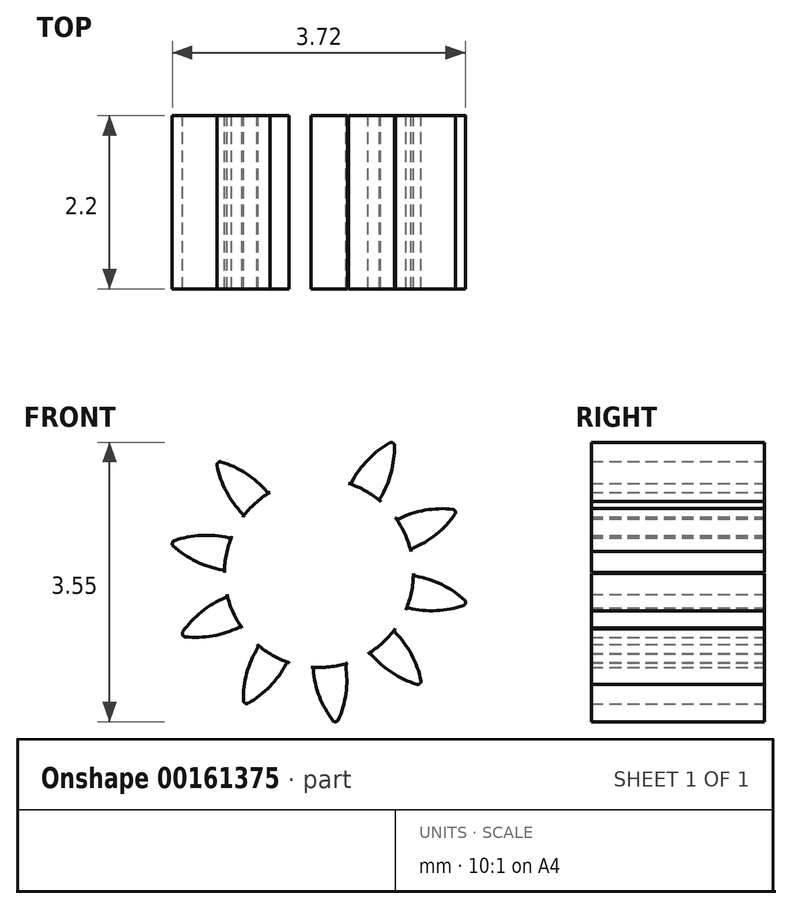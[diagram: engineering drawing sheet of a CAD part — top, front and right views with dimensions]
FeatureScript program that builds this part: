
annotation { "Feature Type Name" : "Feature", "Feature Type Description" : "" }
export const myFeature = defineFeature(function(context is Context, id is Id, definition is map)
    precondition{}
    {
        {
            var Q0;
            Q0=qCreatedBy(makeId("Front.planeOp"),FACE);
            var sketch = newSketch(context, id + "F0", { "sketchPlane" : qUnion([Q0])});
            skCircle(sketch, "E0", {"center": v(0, 0) * mm, "radius": 1.2 * mm, "construction": true});
            skCircle(sketch, "E1", {"center": v(0, 0) * mm, "radius": 1.55 * mm, "construction": true});
            skCircle(sketch, "E2", {"center": v(0, 0) * mm, "radius": 1.9 * mm, "construction": true});
            skLineSegment(sketch, "E3", {"start": v(0, 8.23) * mm, "end": v(0, 0) * mm, "construction": true});
            skCircle(sketch, "E4.cCircle", {"center": v(0, 0) * mm, "radius": 8.23 * mm, "construction": true});
            skLineSegment(sketch, "E4.0", {"start": v(0, 8.23) * mm, "end": v(1.83, 8.03) * mm, "construction": true});
            skLineSegment(sketch, "E4.1", {"start": v(1.83, 8.03) * mm, "end": v(3.57, 7.42) * mm, "construction": true});
            skLineSegment(sketch, "E4.2", {"start": v(3.57, 7.42) * mm, "end": v(5.13, 6.44) * mm, "construction": true});
            skLineSegment(sketch, "E4.3", {"start": v(5.13, 6.44) * mm, "end": v(6.44, 5.13) * mm, "construction": true});
            skLineSegment(sketch, "E4.4", {"start": v(6.44, 5.13) * mm, "end": v(7.42, 3.57) * mm, "construction": true});
            skLineSegment(sketch, "E4.5", {"start": v(7.42, 3.57) * mm, "end": v(8.03, 1.83) * mm, "construction": true});
            skLineSegment(sketch, "E4.6", {"start": v(8.03, 1.83) * mm, "end": v(8.23, 0) * mm, "construction": true});
            skLineSegment(sketch, "E4.7", {"start": v(8.23, 0) * mm, "end": v(8.03, -1.83) * mm, "construction": true});
            skLineSegment(sketch, "E4.8", {"start": v(8.03, -1.83) * mm, "end": v(7.42, -3.57) * mm, "construction": true});
            skLineSegment(sketch, "E4.9", {"start": v(7.42, -3.57) * mm, "end": v(6.44, -5.13) * mm, "construction": true});
            skLineSegment(sketch, "E4.10", {"start": v(6.44, -5.13) * mm, "end": v(5.13, -6.44) * mm, "construction": true});
            skLineSegment(sketch, "E4.11", {"start": v(5.13, -6.44) * mm, "end": v(3.57, -7.42) * mm, "construction": true});
            skLineSegment(sketch, "E4.12", {"start": v(3.57, -7.42) * mm, "end": v(1.83, -8.03) * mm, "construction": true});
            skLineSegment(sketch, "E4.13", {"start": v(1.83, -8.03) * mm, "end": v(0, -8.23) * mm, "construction": true});
            skLineSegment(sketch, "E4.14", {"start": v(0, -8.23) * mm, "end": v(-1.83, -8.03) * mm, "construction": true});
            skLineSegment(sketch, "E4.15", {"start": v(-1.83, -8.03) * mm, "end": v(-3.57, -7.42) * mm, "construction": true});
            skLineSegment(sketch, "E4.16", {"start": v(-3.57, -7.42) * mm, "end": v(-5.13, -6.44) * mm, "construction": true});
            skLineSegment(sketch, "E4.17", {"start": v(-5.13, -6.44) * mm, "end": v(-6.44, -5.13) * mm, "construction": true});
            skLineSegment(sketch, "E4.18", {"start": v(-6.44, -5.13) * mm, "end": v(-7.42, -3.57) * mm, "construction": true});
            skLineSegment(sketch, "E4.19", {"start": v(-7.42, -3.57) * mm, "end": v(-8.03, -1.83) * mm, "construction": true});
            skLineSegment(sketch, "E4.20", {"start": v(-8.03, -1.83) * mm, "end": v(-8.23, 0) * mm, "construction": true});
            skLineSegment(sketch, "E4.21", {"start": v(-8.23, 0) * mm, "end": v(-8.03, 1.83) * mm, "construction": true});
            skLineSegment(sketch, "E4.22", {"start": v(-8.03, 1.83) * mm, "end": v(-7.42, 3.57) * mm, "construction": true});
            skLineSegment(sketch, "E4.23", {"start": v(-7.42, 3.57) * mm, "end": v(-6.44, 5.13) * mm, "construction": true});
            skLineSegment(sketch, "E4.24", {"start": v(-6.44, 5.13) * mm, "end": v(-5.13, 6.44) * mm, "construction": true});
            skLineSegment(sketch, "E4.25", {"start": v(-5.13, 6.44) * mm, "end": v(-3.57, 7.42) * mm, "construction": true});
            skLineSegment(sketch, "E4.26", {"start": v(-3.57, 7.42) * mm, "end": v(-1.83, 8.03) * mm, "construction": true});
            skLineSegment(sketch, "E4.27", {"start": v(-1.83, 8.03) * mm, "end": v(0, 8.23) * mm, "construction": true});
            skLineSegment(sketch, "E5.0", {"start": v(-0.93, 8.23) * mm, "end": v(0.93, 8.23) * mm, "construction": true});
            skLineSegment(sketch, "E5.1", {"start": v(0.93, 8.23) * mm, "end": v(2.74, 7.82) * mm, "construction": true});
            skLineSegment(sketch, "E5.2", {"start": v(2.74, 7.82) * mm, "end": v(4.4, 7.02) * mm, "construction": true});
            skLineSegment(sketch, "E5.3", {"start": v(4.4, 7.02) * mm, "end": v(5.86, 5.86) * mm});
            skLineSegment(sketch, "E5.4", {"start": v(5.86, 5.86) * mm, "end": v(7.02, 4.4) * mm});
            skLineSegment(sketch, "E5.5", {"start": v(7.02, 4.4) * mm, "end": v(7.82, 2.74) * mm});
            skLineSegment(sketch, "E5.6", {"start": v(7.82, 2.74) * mm, "end": v(8.23, 0.93) * mm});
            skLineSegment(sketch, "E5.7", {"start": v(8.23, 0.93) * mm, "end": v(8.23, -0.93) * mm});
            skLineSegment(sketch, "E5.8", {"start": v(8.23, -0.93) * mm, "end": v(7.82, -2.74) * mm});
            skLineSegment(sketch, "E5.9", {"start": v(7.82, -2.74) * mm, "end": v(7.02, -4.4) * mm});
            skLineSegment(sketch, "E5.10", {"start": v(7.02, -4.4) * mm, "end": v(5.86, -5.86) * mm});
            skLineSegment(sketch, "E5.11", {"start": v(5.86, -5.86) * mm, "end": v(4.4, -7.02) * mm});
            skLineSegment(sketch, "E5.12", {"start": v(4.4, -7.02) * mm, "end": v(2.74, -7.82) * mm});
            skLineSegment(sketch, "E5.13", {"start": v(2.74, -7.82) * mm, "end": v(0.93, -8.23) * mm});
            skLineSegment(sketch, "E5.14", {"start": v(0.93, -8.23) * mm, "end": v(-0.93, -8.23) * mm});
            skLineSegment(sketch, "E5.15", {"start": v(-0.93, -8.23) * mm, "end": v(-2.74, -7.82) * mm});
            skLineSegment(sketch, "E5.16", {"start": v(-2.74, -7.82) * mm, "end": v(-4.4, -7.02) * mm});
            skLineSegment(sketch, "E5.17", {"start": v(-4.4, -7.02) * mm, "end": v(-5.86, -5.86) * mm});
            skLineSegment(sketch, "E5.18", {"start": v(-5.86, -5.86) * mm, "end": v(-7.02, -4.4) * mm});
            skLineSegment(sketch, "E5.19", {"start": v(-7.02, -4.4) * mm, "end": v(-7.82, -2.74) * mm});
            skLineSegment(sketch, "E5.20", {"start": v(-7.82, -2.74) * mm, "end": v(-8.23, -0.93) * mm});
            skLineSegment(sketch, "E5.21", {"start": v(-8.23, -0.93) * mm, "end": v(-8.23, 0.93) * mm});
            skLineSegment(sketch, "E5.22", {"start": v(-8.23, 0.93) * mm, "end": v(-7.82, 2.74) * mm});
            skLineSegment(sketch, "E5.23", {"start": v(-7.82, 2.74) * mm, "end": v(-7.02, 4.4) * mm});
            skLineSegment(sketch, "E5.24", {"start": v(-7.02, 4.4) * mm, "end": v(-5.86, 5.86) * mm});
            skLineSegment(sketch, "E5.25", {"start": v(-5.86, 5.86) * mm, "end": v(-4.4, 7.02) * mm, "construction": true});
            skLineSegment(sketch, "E5.26", {"start": v(-4.4, 7.02) * mm, "end": v(-2.74, 7.82) * mm, "construction": true});
            skLineSegment(sketch, "E5.27", {"start": v(-2.74, 7.82) * mm, "end": v(-0.93, 8.23) * mm, "construction": true});
            skPoint(sketch, "E5.0.midPoint", {"position": v(0, 8.23) * mm});
            skLineSegment(sketch, "E6", {"start": v(-0.93, 8.23) * mm, "end": v(0, 0) * mm, "construction": true});
            skLineSegment(sketch, "E7", {"start": v(0, 1.55) * mm, "end": v(-9.32, 1.55) * mm, "construction": true});
            skLineSegment(sketch, "E8", {"start": v(0, 1.55) * mm, "end": v(-4.26, 0) * mm, "construction": true});
            skCircle(sketch, "E9", {"center": v(0, 1.55) * mm, "radius": 1.25 * mm, "construction": true});
            skCircle(sketch, "E10", {"center": v(-1.17, 1.12) * mm, "radius": 1.25 * mm, "construction": true});
            skArc(sketch, "E11", {"start": v(-0.18, 1.88) * mm, "mid": v(0, 1.57) * mm, "end": v(0.07, 1.22) * mm});
            skArc(sketch, "E12.MirrorCS", {"start": v(-0.24, 1.89) * mm, "mid": v(-0.34, 1.53) * mm, "end": v(-0.34, 1.15) * mm});
            skArc(sketch, "E13.MirrorCS", {"start": v(-0.24, 1.87) * mm, "mid": v(-0.34, 1.53) * mm, "end": v(-0.34, 1.18) * mm});
            skArc(sketch, "E14", {"start": v(-0.22, 1.89) * mm, "mid": v(-0.21, 1.89) * mm, "end": v(-0.2, 1.89) * mm});
            skArc(sketch, "E15", {"start": v(-0.36, 1.14) * mm, "mid": v(0.13, -1.2) * mm, "end": v(0.1, 1.2) * mm});
            skPoint(sketch, "E16.visualSharp", {"position": v(-0.34, 1.15) * mm});
            skArc(sketch, "E16.filletArc", {"start": v(-0.36, 1.14) * mm, "mid": v(-0.35, 1.16) * mm, "end": v(-0.34, 1.18) * mm});
            skPoint(sketch, "E17.visualSharp", {"position": v(0.07, 1.2) * mm});
            skArc(sketch, "E17.filletArc", {"start": v(0.07, 1.22) * mm, "mid": v(0.08, 1.2) * mm, "end": v(0.1, 1.2) * mm});
            skPoint(sketch, "E18.visualSharp", {"position": v(-0.24, 1.89) * mm});
            skArc(sketch, "E18.filletArc", {"start": v(-0.22, 1.89) * mm, "mid": v(-0.23, 1.88) * mm, "end": v(-0.24, 1.87) * mm});
            skPoint(sketch, "E19.visualSharp", {"position": v(-0.19, 1.9) * mm});
            skArc(sketch, "E19.filletArc", {"start": v(-0.18, 1.88) * mm, "mid": v(-0.2, 1.89) * mm, "end": v(-0.2, 1.89) * mm});
            skArc(sketch, "E20.1.0", {"start": v(-1.3, 1.37) * mm, "mid": v(-1.18, 1.04) * mm, "end": v(-0.97, 0.75) * mm});
            skArc(sketch, "E20.1.1", {"start": v(-0.97, 0.71) * mm, "mid": v(-0.96, 0.73) * mm, "end": v(-0.97, 0.75) * mm});
            skArc(sketch, "E20.1.2", {"start": v(-1.29, 1.4) * mm, "mid": v(-1.3, 1.38) * mm, "end": v(-1.3, 1.37) * mm});
            skArc(sketch, "E20.1.3", {"start": v(-1.29, 1.4) * mm, "mid": v(-1.28, 1.4) * mm, "end": v(-1.28, 1.4) * mm});
            skArc(sketch, "E20.1.4", {"start": v(-1.25, 1.41) * mm, "mid": v(-0.93, 1.26) * mm, "end": v(-0.66, 1.03) * mm});
            skArc(sketch, "E20.1.5", {"start": v(-1.25, 1.41) * mm, "mid": v(-1.26, 1.41) * mm, "end": v(-1.28, 1.4) * mm});
            skArc(sketch, "E20.1.6", {"start": v(-0.66, 1.03) * mm, "mid": v(-0.64, 1.02) * mm, "end": v(-0.62, 1.03) * mm});
            skArc(sketch, "E20.2.0", {"start": v(-1.85, 0.35) * mm, "mid": v(-1.56, 0.15) * mm, "end": v(-1.23, 0.04) * mm});
            skArc(sketch, "E20.2.1", {"start": v(-1.2, 0) * mm, "mid": v(-1.2, 0.03) * mm, "end": v(-1.23, 0.04) * mm});
            skArc(sketch, "E20.2.2", {"start": v(-1.86, 0.37) * mm, "mid": v(-1.86, 0.36) * mm, "end": v(-1.85, 0.35) * mm});
            skArc(sketch, "E20.2.3", {"start": v(-1.86, 0.37) * mm, "mid": v(-1.86, 0.38) * mm, "end": v(-1.86, 0.39) * mm});
            skArc(sketch, "E20.2.4", {"start": v(-1.84, 0.41) * mm, "mid": v(-1.5, 0.48) * mm, "end": v(-1.14, 0.45) * mm});
            skArc(sketch, "E20.2.5", {"start": v(-1.84, 0.41) * mm, "mid": v(-1.85, 0.4) * mm, "end": v(-1.86, 0.39) * mm});
            skArc(sketch, "E20.2.6", {"start": v(-1.14, 0.45) * mm, "mid": v(-1.12, 0.45) * mm, "end": v(-1.1, 0.46) * mm});
            skArc(sketch, "E20.3.0", {"start": v(-1.7, -0.8) * mm, "mid": v(-1.35, -0.8) * mm, "end": v(-1.01, -0.69) * mm});
            skArc(sketch, "E20.3.1", {"start": v(-0.98, -0.7) * mm, "mid": v(-1, -0.69) * mm, "end": v(-1.01, -0.69) * mm});
            skArc(sketch, "E20.3.2", {"start": v(-1.73, -0.8) * mm, "mid": v(-1.72, -0.8) * mm, "end": v(-1.7, -0.8) * mm});
            skArc(sketch, "E20.3.3", {"start": v(-1.73, -0.8) * mm, "mid": v(-1.73, -0.79) * mm, "end": v(-1.73, -0.78) * mm});
            skArc(sketch, "E20.3.4", {"start": v(-1.73, -0.75) * mm, "mid": v(-1.49, -0.5) * mm, "end": v(-1.19, -0.31) * mm});
            skArc(sketch, "E20.3.5", {"start": v(-1.73, -0.75) * mm, "mid": v(-1.74, -0.76) * mm, "end": v(-1.73, -0.78) * mm});
            skArc(sketch, "E20.3.6", {"start": v(-1.19, -0.31) * mm, "mid": v(-1.17, -0.3) * mm, "end": v(-1.17, -0.27) * mm});
            skArc(sketch, "E20.4.0", {"start": v(-0.9, -1.66) * mm, "mid": v(-0.62, -1.44) * mm, "end": v(-0.42, -1.15) * mm});
            skArc(sketch, "E20.4.1", {"start": v(-0.38, -1.14) * mm, "mid": v(-0.4, -1.14) * mm, "end": v(-0.42, -1.15) * mm});
            skArc(sketch, "E20.4.2", {"start": v(-0.93, -1.66) * mm, "mid": v(-0.92, -1.66) * mm, "end": v(-0.9, -1.66) * mm});
            skArc(sketch, "E20.4.3", {"start": v(-0.93, -1.66) * mm, "mid": v(-0.94, -1.65) * mm, "end": v(-0.94, -1.65) * mm});
            skArc(sketch, "E20.4.4", {"start": v(-0.96, -1.62) * mm, "mid": v(-0.92, -1.27) * mm, "end": v(-0.78, -0.95) * mm});
            skArc(sketch, "E20.4.5", {"start": v(-0.96, -1.62) * mm, "mid": v(-0.95, -1.64) * mm, "end": v(-0.94, -1.65) * mm});
            skArc(sketch, "E20.4.6", {"start": v(-0.78, -0.95) * mm, "mid": v(-0.77, -0.93) * mm, "end": v(-0.78, -0.9) * mm});
            skArc(sketch, "E20.5.0", {"start": v(0.24, -1.87) * mm, "mid": v(0.34, -1.53) * mm, "end": v(0.34, -1.18) * mm});
            skArc(sketch, "E20.5.1", {"start": v(0.36, -1.14) * mm, "mid": v(0.35, -1.16) * mm, "end": v(0.34, -1.18) * mm});
            skArc(sketch, "E20.5.2", {"start": v(0.22, -1.89) * mm, "mid": v(0.23, -1.88) * mm, "end": v(0.24, -1.87) * mm});
            skArc(sketch, "E20.5.3", {"start": v(0.22, -1.89) * mm, "mid": v(0.21, -1.89) * mm, "end": v(0.2, -1.89) * mm});
            skArc(sketch, "E20.5.4", {"start": v(0.18, -1.88) * mm, "mid": v(0, -1.57) * mm, "end": v(-0.07, -1.22) * mm});
            skArc(sketch, "E20.5.5", {"start": v(0.18, -1.88) * mm, "mid": v(0.2, -1.89) * mm, "end": v(0.2, -1.89) * mm});
            skArc(sketch, "E20.5.6", {"start": v(-0.07, -1.22) * mm, "mid": v(-0.08, -1.2) * mm, "end": v(-0.1, -1.2) * mm});
            skArc(sketch, "E20.6.0", {"start": v(1.3, -1.37) * mm, "mid": v(1.18, -1.04) * mm, "end": v(0.97, -0.75) * mm});
            skArc(sketch, "E20.6.1", {"start": v(0.97, -0.71) * mm, "mid": v(0.96, -0.73) * mm, "end": v(0.97, -0.75) * mm});
            skArc(sketch, "E20.6.2", {"start": v(1.29, -1.4) * mm, "mid": v(1.3, -1.38) * mm, "end": v(1.3, -1.37) * mm});
            skArc(sketch, "E20.6.3", {"start": v(1.29, -1.4) * mm, "mid": v(1.28, -1.4) * mm, "end": v(1.28, -1.4) * mm});
            skArc(sketch, "E20.6.4", {"start": v(1.25, -1.41) * mm, "mid": v(0.93, -1.26) * mm, "end": v(0.66, -1.03) * mm});
            skArc(sketch, "E20.6.5", {"start": v(1.25, -1.41) * mm, "mid": v(1.26, -1.41) * mm, "end": v(1.28, -1.4) * mm});
            skArc(sketch, "E20.6.6", {"start": v(0.66, -1.03) * mm, "mid": v(0.64, -1.02) * mm, "end": v(0.62, -1.03) * mm});
            skArc(sketch, "E20.7.0", {"start": v(1.85, -0.35) * mm, "mid": v(1.56, -0.15) * mm, "end": v(1.23, -0.04) * mm});
            skArc(sketch, "E20.7.1", {"start": v(1.2, 0) * mm, "mid": v(1.2, -0.03) * mm, "end": v(1.23, -0.04) * mm});
            skArc(sketch, "E20.7.2", {"start": v(1.86, -0.37) * mm, "mid": v(1.86, -0.36) * mm, "end": v(1.85, -0.35) * mm});
            skArc(sketch, "E20.7.3", {"start": v(1.86, -0.37) * mm, "mid": v(1.86, -0.38) * mm, "end": v(1.86, -0.39) * mm});
            skArc(sketch, "E20.7.4", {"start": v(1.84, -0.41) * mm, "mid": v(1.5, -0.48) * mm, "end": v(1.14, -0.45) * mm});
            skArc(sketch, "E20.7.5", {"start": v(1.84, -0.41) * mm, "mid": v(1.85, -0.4) * mm, "end": v(1.86, -0.39) * mm});
            skArc(sketch, "E20.7.6", {"start": v(1.14, -0.45) * mm, "mid": v(1.12, -0.45) * mm, "end": v(1.1, -0.46) * mm});
            skArc(sketch, "E20.8.0", {"start": v(1.7, 0.8) * mm, "mid": v(1.35, 0.8) * mm, "end": v(1.01, 0.69) * mm});
            skArc(sketch, "E20.8.1", {"start": v(0.98, 0.7) * mm, "mid": v(1, 0.69) * mm, "end": v(1.01, 0.69) * mm});
            skArc(sketch, "E20.8.2", {"start": v(1.73, 0.8) * mm, "mid": v(1.72, 0.8) * mm, "end": v(1.7, 0.8) * mm});
            skArc(sketch, "E20.8.3", {"start": v(1.73, 0.8) * mm, "mid": v(1.73, 0.79) * mm, "end": v(1.73, 0.78) * mm});
            skArc(sketch, "E20.8.4", {"start": v(1.73, 0.75) * mm, "mid": v(1.49, 0.5) * mm, "end": v(1.19, 0.31) * mm});
            skArc(sketch, "E20.8.5", {"start": v(1.73, 0.75) * mm, "mid": v(1.74, 0.76) * mm, "end": v(1.73, 0.78) * mm});
            skArc(sketch, "E20.8.6", {"start": v(1.19, 0.31) * mm, "mid": v(1.17, 0.3) * mm, "end": v(1.17, 0.27) * mm});
            skArc(sketch, "E20.9.0", {"start": v(0.9, 1.66) * mm, "mid": v(0.62, 1.44) * mm, "end": v(0.42, 1.15) * mm});
            skArc(sketch, "E20.9.1", {"start": v(0.38, 1.14) * mm, "mid": v(0.4, 1.14) * mm, "end": v(0.42, 1.15) * mm});
            skArc(sketch, "E20.9.2", {"start": v(0.93, 1.66) * mm, "mid": v(0.92, 1.66) * mm, "end": v(0.9, 1.66) * mm});
            skArc(sketch, "E20.9.3", {"start": v(0.93, 1.66) * mm, "mid": v(0.94, 1.65) * mm, "end": v(0.94, 1.65) * mm});
            skArc(sketch, "E20.9.4", {"start": v(0.96, 1.62) * mm, "mid": v(0.92, 1.27) * mm, "end": v(0.78, 0.95) * mm});
            skArc(sketch, "E20.9.5", {"start": v(0.96, 1.62) * mm, "mid": v(0.95, 1.64) * mm, "end": v(0.94, 1.65) * mm});
            skArc(sketch, "E20.9.6", {"start": v(0.78, 0.95) * mm, "mid": v(0.77, 0.93) * mm, "end": v(0.78, 0.9) * mm});
            skSolve(sketch);
        }
        {
            var Q0;
            Q0=makeQuery(id+"F0.imprint","IMPRINT",FACE,{"disambiguationData":[TD([[makeQuery(id+"F0.imprint","IMPRINT",EDGE,{"derivedFrom":sQuery(id+"F0.wireOp",EDGE,"E11")}),-1.0]])]});
            var Q1;
            Q1=makeQuery(id+"F0.imprint","IMPRINT",FACE,{"disambiguationData":[TD([[makeQuery(id+"F0.imprint","IMPRINT",EDGE,{"derivedFrom":sQuery(id+"F0.wireOp",EDGE,"E20.1.0")}),1.0]])]});
            var Q2;
            Q2=makeQuery(id+"F0.imprint","IMPRINT",FACE,{"disambiguationData":[TD([[makeQuery(id+"F0.imprint","IMPRINT",EDGE,{"derivedFrom":sQuery(id+"F0.wireOp",EDGE,"E20.3.0")}),1.0]])]});
            var Q3;
            Q3=makeQuery(id+"F0.imprint","IMPRINT",FACE,{"disambiguationData":[TD([[makeQuery(id+"F0.imprint","IMPRINT",EDGE,{"derivedFrom":sQuery(id+"F0.wireOp",EDGE,"E20.5.0")}),1.0]])]});
            var Q4;
            Q4=makeQuery(id+"F0.imprint","IMPRINT",FACE,{"disambiguationData":[TD([[makeQuery(id+"F0.imprint","IMPRINT",EDGE,{"derivedFrom":sQuery(id+"F0.wireOp",EDGE,"E20.6.0")}),1.0]])]});
            var Q5;
            Q5=makeQuery(id+"F0.imprint","IMPRINT",FACE,{"disambiguationData":[TD([[makeQuery(id+"F0.imprint","IMPRINT",EDGE,{"derivedFrom":sQuery(id+"F0.wireOp",EDGE,"E20.7.0")}),1.0]])]});
            var Q6;
            Q6=makeQuery(id+"F0.imprint","IMPRINT",FACE,{"disambiguationData":[TD([[makeQuery(id+"F0.imprint","IMPRINT",EDGE,{"derivedFrom":sQuery(id+"F0.wireOp",EDGE,"E20.8.0")}),1.0]])]});
            var Q7;
            Q7=makeQuery(id+"F0.imprint","IMPRINT",FACE,{"disambiguationData":[TD([[makeQuery(id+"F0.imprint","IMPRINT",EDGE,{"derivedFrom":sQuery(id+"F0.wireOp",EDGE,"E20.9.0")}),1.0]])]});
            var Q8;
            Q8=makeQuery(id+"F0.imprint","IMPRINT",FACE,{"disambiguationData":[TD([[makeQuery(id+"F0.imprint","IMPRINT",EDGE,{"derivedFrom":sQuery(id+"F0.wireOp",EDGE,"E20.10.0")}),1.0]])]});
            var Q9;
            Q9=makeQuery(id+"F0.imprint","IMPRINT",FACE,{"disambiguationData":[TD([[makeQuery(id+"F0.imprint","IMPRINT",EDGE,{"derivedFrom":sQuery(id+"F0.wireOp",EDGE,"E20.11.0")}),1.0]])]});
            var Q10;
            Q10=makeQuery(id+"F0.imprint","IMPRINT",FACE,{"disambiguationData":[TD([[makeQuery(id+"F0.imprint","IMPRINT",EDGE,{"derivedFrom":sQuery(id+"F0.wireOp",EDGE,"E20.12.0")}),1.0]])]});
            var Q11;
            Q11=makeQuery(id+"F0.imprint","IMPRINT",FACE,{"disambiguationData":[TD([[makeQuery(id+"F0.imprint","IMPRINT",EDGE,{"derivedFrom":sQuery(id+"F0.wireOp",EDGE,"E20.13.0")}),1.0]])]});
            var Q12;
            Q12=makeQuery(id+"F0.imprint","IMPRINT",FACE,{"disambiguationData":[TD([[makeQuery(id+"F0.imprint","IMPRINT",EDGE,{"derivedFrom":sQuery(id+"F0.wireOp",EDGE,"E20.2.0")}),1.0]])]});
            var Q13;
            Q13=makeQuery(id+"F0.imprint","IMPRINT",FACE,{"disambiguationData":[TD([[makeQuery(id+"F0.imprint","IMPRINT",EDGE,{"derivedFrom":sQuery(id+"F0.wireOp",EDGE,"E20.4.0")}),1.0]])]});
            extrude(context, id + "F1", {"entities" : qUnion([Q0, Q1, Q2, Q3, Q4, Q5, Q6, Q7, Q8, Q9, Q10, Q11, Q12, Q13]), "depth" : 2.2 * mm});
        }
        {
            var Q0;
            Q0=makeQuery(id+"F1.opExtrude","CAP_FACE",FACE,{"disambiguationData":[OSD([sQuery(id+"F0.wireOp",EDGE,"E11"),sQuery(id+"F0.wireOp",EDGE,"E13.MirrorCS"),sQuery(id+"F0.wireOp",EDGE,"E14"),sQuery(id+"F0.wireOp",EDGE,"E15"),sQuery(id+"F0.wireOp",EDGE,"E16.filletArc"),sQuery(id+"F0.wireOp",EDGE,"E17.filletArc"),sQuery(id+"F0.wireOp",EDGE,"E18.filletArc"),sQuery(id+"F0.wireOp",EDGE,"E19.filletArc"),sQuery(id+"F0.wireOp",EDGE,"E20.1.0"),sQuery(id+"F0.wireOp",EDGE,"E20.1.1"),sQuery(id+"F0.wireOp",EDGE,"E20.1.2"),sQuery(id+"F0.wireOp",EDGE,"E20.1.3"),sQuery(id+"F0.wireOp",EDGE,"E20.1.4"),sQuery(id+"F0.wireOp",EDGE,"E20.1.5"),sQuery(id+"F0.wireOp",EDGE,"E20.1.6"),sQuery(id+"F0.wireOp",EDGE,"E20.2.0"),sQuery(id+"F0.wireOp",EDGE,"E20.2.1"),sQuery(id+"F0.wireOp",EDGE,"E20.2.2"),sQuery(id+"F0.wireOp",EDGE,"E20.2.3"),sQuery(id+"F0.wireOp",EDGE,"E20.2.4"),sQuery(id+"F0.wireOp",EDGE,"E20.2.5"),sQuery(id+"F0.wireOp",EDGE,"E20.2.6"),sQuery(id+"F0.wireOp",EDGE,"E20.3.0"),sQuery(id+"F0.wireOp",EDGE,"E20.3.1"),sQuery(id+"F0.wireOp",EDGE,"E20.3.2"),sQuery(id+"F0.wireOp",EDGE,"E20.3.3"),sQuery(id+"F0.wireOp",EDGE,"E20.3.4"),sQuery(id+"F0.wireOp",EDGE,"E20.3.5"),sQuery(id+"F0.wireOp",EDGE,"E20.3.6"),sQuery(id+"F0.wireOp",EDGE,"E20.4.0"),sQuery(id+"F0.wireOp",EDGE,"E20.4.1"),sQuery(id+"F0.wireOp",EDGE,"E20.4.2"),sQuery(id+"F0.wireOp",EDGE,"E20.4.3"),sQuery(id+"F0.wireOp",EDGE,"E20.4.4"),sQuery(id+"F0.wireOp",EDGE,"E20.4.5"),sQuery(id+"F0.wireOp",EDGE,"E20.4.6"),sQuery(id+"F0.wireOp",EDGE,"E20.5.0"),sQuery(id+"F0.wireOp",EDGE,"E20.5.1"),sQuery(id+"F0.wireOp",EDGE,"E20.5.2"),sQuery(id+"F0.wireOp",EDGE,"E20.5.3"),sQuery(id+"F0.wireOp",EDGE,"E20.5.4"),sQuery(id+"F0.wireOp",EDGE,"E20.5.5"),sQuery(id+"F0.wireOp",EDGE,"E20.5.6"),sQuery(id+"F0.wireOp",EDGE,"E20.6.0"),sQuery(id+"F0.wireOp",EDGE,"E20.6.1"),sQuery(id+"F0.wireOp",EDGE,"E20.6.2"),sQuery(id+"F0.wireOp",EDGE,"E20.6.3"),sQuery(id+"F0.wireOp",EDGE,"E20.6.4"),sQuery(id+"F0.wireOp",EDGE,"E20.6.5"),sQuery(id+"F0.wireOp",EDGE,"E20.6.6"),sQuery(id+"F0.wireOp",EDGE,"E20.7.0"),sQuery(id+"F0.wireOp",EDGE,"E20.7.1"),sQuery(id+"F0.wireOp",EDGE,"E20.7.2"),sQuery(id+"F0.wireOp",EDGE,"E20.7.3"),sQuery(id+"F0.wireOp",EDGE,"E20.7.4"),sQuery(id+"F0.wireOp",EDGE,"E20.7.5"),sQuery(id+"F0.wireOp",EDGE,"E20.7.6"),sQuery(id+"F0.wireOp",EDGE,"E20.8.0"),sQuery(id+"F0.wireOp",EDGE,"E20.8.1"),sQuery(id+"F0.wireOp",EDGE,"E20.8.2"),sQuery(id+"F0.wireOp",EDGE,"E20.8.3"),sQuery(id+"F0.wireOp",EDGE,"E20.8.4"),sQuery(id+"F0.wireOp",EDGE,"E20.8.5"),sQuery(id+"F0.wireOp",EDGE,"E20.8.6"),sQuery(id+"F0.wireOp",EDGE,"E20.9.0"),sQuery(id+"F0.wireOp",EDGE,"E20.9.1"),sQuery(id+"F0.wireOp",EDGE,"E20.9.2"),sQuery(id+"F0.wireOp",EDGE,"E20.9.3"),sQuery(id+"F0.wireOp",EDGE,"E20.9.4"),sQuery(id+"F0.wireOp",EDGE,"E20.9.5"),sQuery(id+"F0.wireOp",EDGE,"E20.9.6"),sQuery(id+"F0.wireOp",EDGE,"E20.10.0"),sQuery(id+"F0.wireOp",EDGE,"E20.10.1"),sQuery(id+"F0.wireOp",EDGE,"E20.10.2"),sQuery(id+"F0.wireOp",EDGE,"E20.10.3"),sQuery(id+"F0.wireOp",EDGE,"E20.10.4"),sQuery(id+"F0.wireOp",EDGE,"E20.10.5"),sQuery(id+"F0.wireOp",EDGE,"E20.10.6"),sQuery(id+"F0.wireOp",EDGE,"E20.11.0"),sQuery(id+"F0.wireOp",EDGE,"E20.11.1"),sQuery(id+"F0.wireOp",EDGE,"E20.11.2"),sQuery(id+"F0.wireOp",EDGE,"E20.11.3"),sQuery(id+"F0.wireOp",EDGE,"E20.11.4"),sQuery(id+"F0.wireOp",EDGE,"E20.11.5"),sQuery(id+"F0.wireOp",EDGE,"E20.11.6"),sQuery(id+"F0.wireOp",EDGE,"E20.12.0"),sQuery(id+"F0.wireOp",EDGE,"E20.12.1"),sQuery(id+"F0.wireOp",EDGE,"E20.12.2"),sQuery(id+"F0.wireOp",EDGE,"E20.12.3"),sQuery(id+"F0.wireOp",EDGE,"E20.12.4"),sQuery(id+"F0.wireOp",EDGE,"E20.12.5"),sQuery(id+"F0.wireOp",EDGE,"E20.12.6"),sQuery(id+"F0.wireOp",EDGE,"E20.13.0"),sQuery(id+"F0.wireOp",EDGE,"E20.13.1"),sQuery(id+"F0.wireOp",EDGE,"E20.13.2"),sQuery(id+"F0.wireOp",EDGE,"E20.13.3"),sQuery(id+"F0.wireOp",EDGE,"E20.13.4"),sQuery(id+"F0.wireOp",EDGE,"E20.13.5"),sQuery(id+"F0.wireOp",EDGE,"E20.13.6")])],"isStart":false});
            var sketch = newSketch(context, id + "F2", { "sketchPlane" : qUnion([Q0])});
            skCircle(sketch, "E21", {"center": v(0, 0) * mm, "radius": 1.1 * mm});
            skSolve(sketch);
        }
        {
            var Q0;
            Q0=qSketchRegion(id+"F2",true);
            extrude(context, id + "F3", {"entities" : qUnion([Q0]), "operationType" : NewBodyOperationType.REMOVE, "endBound" : BoundingType.THROUGH_ALL, "oppositeDirection" : true, "depth" : 25 * mm});
        }
    });
